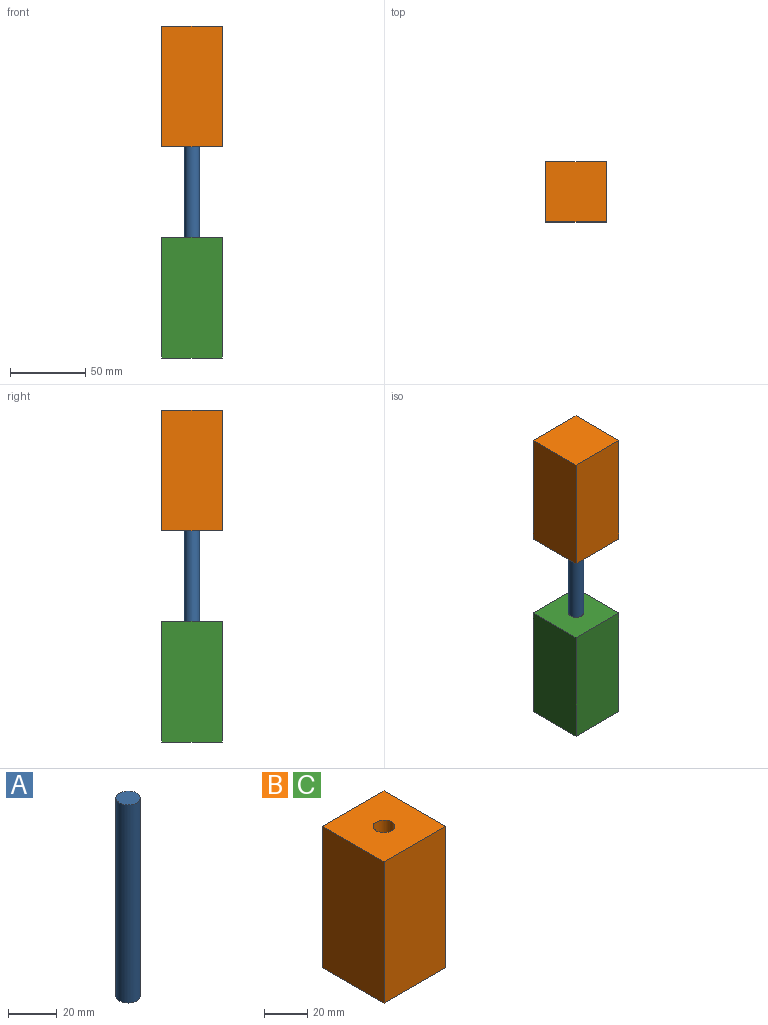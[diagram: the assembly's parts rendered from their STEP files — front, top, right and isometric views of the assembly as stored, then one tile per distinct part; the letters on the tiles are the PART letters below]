
ASSEMBLY  parts=3 mates=3
PART A: 3 faces, bbox 10x10x100 mm
  f0: cylinder r=5mm len=100mm, axis (0,0,1), area 3141.6mm2, adj f1,f2
  f1: plane 10x10mm, normal (0,0,1), area 78.5mm2, adj f0
  f2: plane 10x10mm, normal (0,0,-1), area 78.5mm2, adj f0
PART B: 8 faces, bbox 40x40x80 mm
  f0: plane 80x40mm, normal (-1,0,0), area 3200mm2, adj f1,f3,f4,f5
  f1: plane 80x40mm, normal (0,-1,0), area 3200mm2, adj f0,f2,f4,f5
  f2: plane 80x40mm, normal (1,0,0), area 3200mm2, adj f1,f3,f4,f5
  f3: plane 80x40mm, normal (0,1,0), area 3200mm2, adj f0,f2,f4,f5
  f4: plane 40x40mm, normal (0,0,1), area 1521.5mm2, adj f0,f1,f2,f3,f6
  f5: plane 40x40mm, normal (0,0,-1), area 1600mm2, adj f0,f1,f2,f3
  f6: cylinder r=5mm len=20mm, axis (0,0,1), area 628.3mm2, adj f4,f7
  f7: plane 10x10mm, normal (0,0,1), area 78.5mm2, adj f6
PART C: same geometry as B
PLACE A t=(-48.54,-82.47,192.85)mm
PLACE B rot(axis=(1,0,0),180deg) t=(-48.54,-82.47,172.85)mm
PLACE C t=(-48.54,-82.47,112.85)mm
MATE fastened B.f6 <-> A.f0  axis (0,0,-1) through (-48.54,-82.47,192.85)mm
MATE fastened A.f0 <-> C.f6  axis (0,0,-1) through (-48.54,-82.47,92.85)mm
MATE parallel B.f6 <-> C.f6  axis (0,0,-1) through (-48.54,-82.47,172.85)mm
